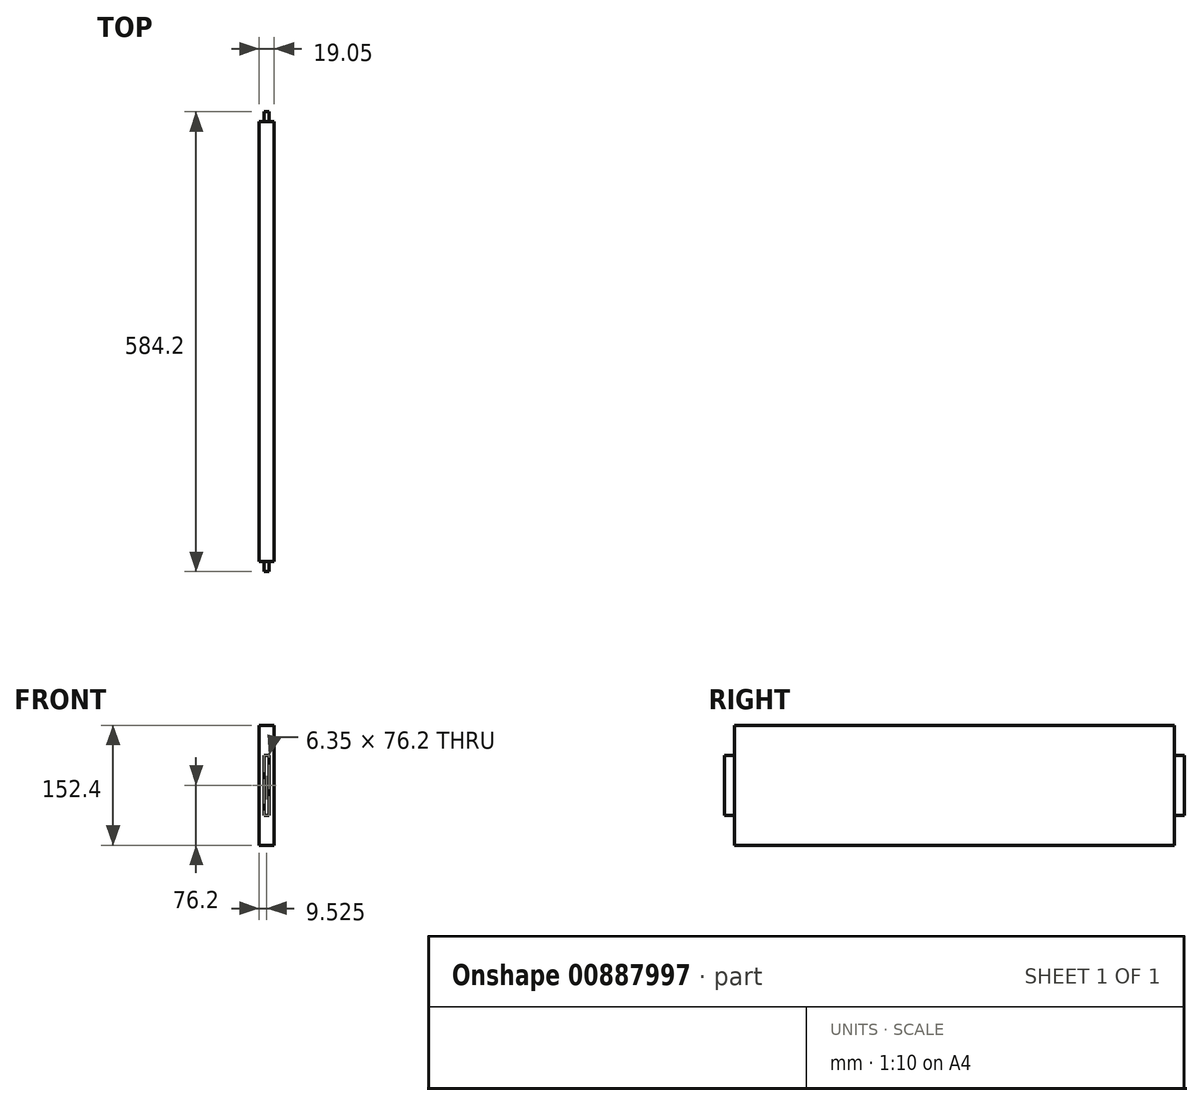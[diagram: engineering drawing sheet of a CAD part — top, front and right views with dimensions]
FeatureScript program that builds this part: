
annotation { "Feature Type Name" : "Feature", "Feature Type Description" : "" }
export const myFeature = defineFeature(function(context is Context, id is Id, definition is map)
    precondition{}
    {
        {
            var Q0;
            Q0=qCreatedBy(makeId("Right.planeOp"),FACE);
            var sketch = newSketch(context, id + "F0", { "sketchPlane" : qUnion([Q0])});
            skLineSegment(sketch, "E0.bottom", {"start": v(279.4, -76.2) * mm, "end": v(-279.4, -76.2) * mm});
            skLineSegment(sketch, "E0.top", {"start": v(279.4, 76.2) * mm, "end": v(-279.4, 76.2) * mm});
            skLineSegment(sketch, "E0.left", {"start": v(292.1, -38.1) * mm, "end": v(292.1, 38.1) * mm});
            skLineSegment(sketch, "E0.right", {"start": v(-292.1, -38.1) * mm, "end": v(-292.1, 38.1) * mm});
            skPoint(sketch, "E0.middle", {"position": v(0, 0) * mm});
            skLineSegment(sketch, "E1.top", {"start": v(292.1, 38.1) * mm, "end": v(279.4, 38.1) * mm});
            skLineSegment(sketch, "E1.right", {"start": v(279.4, 76.2) * mm, "end": v(279.4, 38.1) * mm});
            skPoint(sketch, "E1.bottom.start.orphan", {"position": v(292.1, 76.2) * mm});
            skLineSegment(sketch, "E2.top", {"start": v(292.1, -38.1) * mm, "end": v(279.4, -38.1) * mm});
            skLineSegment(sketch, "E2.right", {"start": v(279.4, -76.2) * mm, "end": v(279.4, -38.1) * mm});
            skPoint(sketch, "E3.orphan", {"position": v(292.1, -76.2) * mm});
            skLineSegment(sketch, "E4.top", {"start": v(-292.1, 38.1) * mm, "end": v(-279.4, 38.1) * mm});
            skLineSegment(sketch, "E4.right", {"start": v(-279.4, 76.2) * mm, "end": v(-279.4, 38.1) * mm});
            skPoint(sketch, "E4.bottom.start.orphan", {"position": v(-292.1, 76.2) * mm});
            skLineSegment(sketch, "E5.top", {"start": v(-292.1, -38.1) * mm, "end": v(-279.4, -38.1) * mm});
            skLineSegment(sketch, "E5.right", {"start": v(-279.4, -76.2) * mm, "end": v(-279.4, -38.1) * mm});
            skPoint(sketch, "E5.bottom.start.orphan", {"position": v(-292.1, -76.2) * mm});
            skSolve(sketch);
        }
        {
            var Q0;
            Q0 = qSketchRegion(id + "F0", true);
            extrude(context, id + "F1", {"entities" : qUnion([Q0]), "depth" : 19.05 * mm, "offsetDistance" : 25.4 * mm});
        }
        {
            var Q0;
            Q0=makeQuery(id+"F1.opExtrude","SWEPT_FACE",FACE,{"disambiguationData":[OSD([sQuery(id+"F0.wireOp",EDGE,"E0.right")])]});
            var sketch = newSketch(context, id + "F2", { "sketchPlane" : qUnion([Q0])});
            skLineSegment(sketch, "E6.bottom", {"start": v(19.05, 38.1) * mm, "end": v(12.7, 38.1) * mm});
            skLineSegment(sketch, "E6.top", {"start": v(19.05, -38.1) * mm, "end": v(12.7, -38.1) * mm});
            skLineSegment(sketch, "E6.left", {"start": v(19.05, 38.1) * mm, "end": v(19.05, -38.1) * mm});
            skLineSegment(sketch, "E6.right", {"start": v(12.7, 38.1) * mm, "end": v(12.7, -38.1) * mm});
            skLineSegment(sketch, "E7.bottom", {"start": v(0, 38.1) * mm, "end": v(6.35, 38.1) * mm});
            skLineSegment(sketch, "E7.top", {"start": v(0, -38.1) * mm, "end": v(6.35, -38.1) * mm});
            skLineSegment(sketch, "E7.left", {"start": v(0, 38.1) * mm, "end": v(0, -38.1) * mm});
            skLineSegment(sketch, "E7.right", {"start": v(6.35, 38.1) * mm, "end": v(6.35, -38.1) * mm});
            skSolve(sketch);
        }
        {
            var Q0;
            Q0 = qSketchRegion(id + "F2", true);
            extrude(context, id + "F3", {"entities" : qUnion([Q0]), "operationType" : NewBodyOperationType.REMOVE, "oppositeDirection" : true, "depth" : 12.7 * mm, "offsetDistance" : 25.4 * mm});
        }
        {
            var Q0;
            Q0=makeQuery(id+"F1.opExtrude","SWEPT_FACE",FACE,{"disambiguationData":[OSD([sQuery(id+"F0.wireOp",EDGE,"E0.left")])]});
            var sketch = newSketch(context, id + "F4", { "sketchPlane" : qUnion([Q0])});
            skLineSegment(sketch, "E8.bottom", {"start": v(0, 38.1) * mm, "end": v(-6.35, 38.1) * mm});
            skLineSegment(sketch, "E8.top", {"start": v(0, -38.1) * mm, "end": v(-6.35, -38.1) * mm});
            skLineSegment(sketch, "E8.left", {"start": v(0, 38.1) * mm, "end": v(0, -38.1) * mm});
            skLineSegment(sketch, "E8.right", {"start": v(-6.35, 38.1) * mm, "end": v(-6.35, -38.1) * mm});
            skLineSegment(sketch, "E9.bottom", {"start": v(-19.05, 38.1) * mm, "end": v(-12.7, 38.1) * mm});
            skLineSegment(sketch, "E9.top", {"start": v(-19.05, -38.1) * mm, "end": v(-12.7, -38.1) * mm});
            skLineSegment(sketch, "E9.left", {"start": v(-19.05, 38.1) * mm, "end": v(-19.05, -38.1) * mm});
            skLineSegment(sketch, "E9.right", {"start": v(-12.7, 38.1) * mm, "end": v(-12.7, -38.1) * mm});
            skSolve(sketch);
        }
        {
            var Q0;
            Q0 = qSketchRegion(id + "F4", true);
            extrude(context, id + "F5", {"entities" : qUnion([Q0]), "operationType" : NewBodyOperationType.REMOVE, "oppositeDirection" : true, "depth" : 12.7 * mm, "offsetDistance" : 25.4 * mm});
        }
    });
